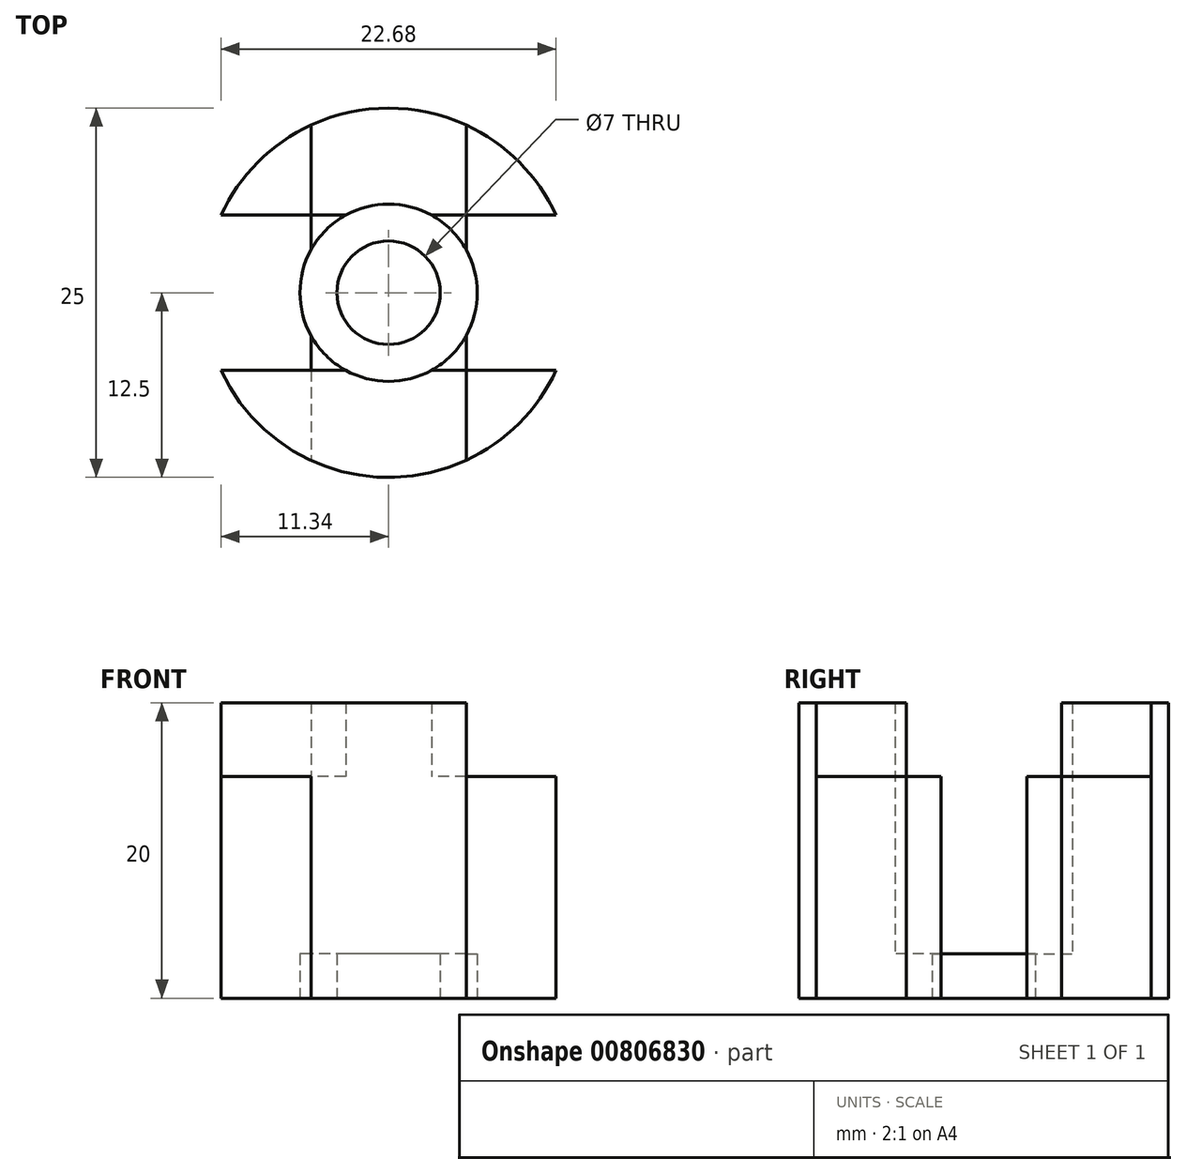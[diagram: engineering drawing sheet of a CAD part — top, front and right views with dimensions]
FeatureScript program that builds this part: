
annotation { "Feature Type Name" : "Feature", "Feature Type Description" : "" }
export const myFeature = defineFeature(function(context is Context, id is Id, definition is map)
    precondition{}
    {
        {
            var Q0;
            Q0=qCreatedBy(makeId("Top.planeOp"),FACE);
            var sketch = newSketch(context, id + "F0", { "sketchPlane" : qUnion([Q0])});
            skCircle(sketch, "E0", {"center": v(0, 0) * mm, "radius": 12.5 * mm});
            skCircle(sketch, "E1", {"center": v(0, 0) * mm, "radius": 6 * mm});
            skLineSegment(sketch, "E2.bottom", {"start": v(5.25, 21.3) * mm, "end": v(-5.25, 21.3) * mm});
            skLineSegment(sketch, "E2.top", {"start": v(5.25, -21.3) * mm, "end": v(-5.25, -21.3) * mm});
            skLineSegment(sketch, "E2.left", {"start": v(5.25, 21.3) * mm, "end": v(5.25, -21.3) * mm});
            skLineSegment(sketch, "E2.right", {"start": v(-5.25, 21.3) * mm, "end": v(-5.25, -21.3) * mm});
            skLineSegment(sketch, "E3.bottom", {"start": v(25.07, 5.25) * mm, "end": v(-25.07, 5.25) * mm});
            skLineSegment(sketch, "E3.top", {"start": v(25.07, -5.25) * mm, "end": v(-25.07, -5.25) * mm});
            skLineSegment(sketch, "E3.left", {"start": v(25.07, 5.25) * mm, "end": v(25.07, -5.25) * mm});
            skLineSegment(sketch, "E3.right", {"start": v(-25.07, 5.25) * mm, "end": v(-25.07, -5.25) * mm});
            skCircle(sketch, "E4", {"center": v(0, 0) * mm, "radius": 3.5 * mm});
            skSolve(sketch);
        }
        {
            var Q0;
            Q0=makeQuery(id+"F0.imprint","IMPRINT",FACE,{"disambiguationData":[TD([[makeQuery(id+"F0.imprint","IMPRINT",EDGE,{"derivedFrom":sQuery(id+"F0.wireOp",EDGE,"E0")}),1.0]])]});
            var Q1;
            {var subQ0=sQuery(id+"F0.wireOp",EDGE,"E3.bottom");var subQ1=sQuery(id+"F0.wireOp",EDGE,"E0");var subQ2=makeQuery(id+"F0.imprint","INTERSECT",VERTEX,{"disambiguationData":[OD(1.0)],"derivedFrom":[subQ1,subQ0]});Q1=makeQuery(id+"F0.imprint","IMPRINT",FACE,{"disambiguationData":[TD([[makeQuery(id+"F0.imprint","IMPRINT",EDGE,{"disambiguationData":[TD([[subQ2,-1.0]])],"derivedFrom":subQ1}),1.0]])]});}
            var Q2;
            {var subQ0=sQuery(id+"F0.wireOp",EDGE,"E2.right");var subQ1=sQuery(id+"F0.wireOp",EDGE,"E0");var subQ2=makeQuery(id+"F0.imprint","INTERSECT",VERTEX,{"disambiguationData":[OD(1.0)],"derivedFrom":[subQ1,subQ0]});Q2=makeQuery(id+"F0.imprint","IMPRINT",FACE,{"disambiguationData":[TD([[makeQuery(id+"F0.imprint","IMPRINT",EDGE,{"disambiguationData":[TD([[subQ2,-1.0]])],"derivedFrom":subQ1}),1.0]])]});}
            var Q3;
            {var subQ0=sQuery(id+"F0.wireOp",EDGE,"E3.bottom");var subQ1=sQuery(id+"F0.wireOp",EDGE,"E0");var subQ2=makeQuery(id+"F0.imprint","INTERSECT",VERTEX,{"disambiguationData":[OD(0.0)],"derivedFrom":[subQ1,subQ0]});Q3=makeQuery(id+"F0.imprint","IMPRINT",FACE,{"disambiguationData":[TD([[makeQuery(id+"F0.imprint","IMPRINT",EDGE,{"disambiguationData":[TD([[subQ2,1.0]])],"derivedFrom":subQ1}),1.0]])]});}
            var Q4;
            {var subQ0=sQuery(id+"F0.wireOp",EDGE,"E2.left");var subQ1=sQuery(id+"F0.wireOp",EDGE,"E0");var subQ2=makeQuery(id+"F0.imprint","INTERSECT",VERTEX,{"disambiguationData":[OD(0.0)],"derivedFrom":[subQ1,subQ0]});Q4=makeQuery(id+"F0.imprint","IMPRINT",FACE,{"disambiguationData":[TD([[makeQuery(id+"F0.imprint","IMPRINT",EDGE,{"disambiguationData":[TD([[subQ2,-1.0]])],"derivedFrom":subQ1}),1.0]])]});}
            var Q5;
            Q5=makeQuery(id+"F0.imprint","IMPRINT",FACE,{"disambiguationData":[TD([[makeQuery(id+"F0.imprint","IMPRINT",EDGE,{"derivedFrom":sQuery(id+"F0.wireOp",EDGE,"E1")}),-1.0]])]});
            extrude(context, id + "F1", {"entities" : qUnion([Q0, Q1, Q2, Q3, Q4, Q5]), "depth" : 15 * mm, "offsetDistance" : 25 * mm});
        }
        {
            var Q0;
            {var subQ0=sQuery(id+"F0.wireOp",EDGE,"E2.right");var subQ1=sQuery(id+"F0.wireOp",EDGE,"E0");var subQ2=makeQuery(id+"F0.imprint","INTERSECT",VERTEX,{"disambiguationData":[OD(0.0)],"derivedFrom":[subQ1,subQ0]});Q0=makeQuery(id+"F0.imprint","IMPRINT",FACE,{"disambiguationData":[TD([[makeQuery(id+"F0.imprint","IMPRINT",EDGE,{"disambiguationData":[TD([[subQ2,-1.0]])],"derivedFrom":subQ1}),1.0]])]});}
            var Q1;
            {var subQ0=sQuery(id+"F0.wireOp",EDGE,"E3.top");var subQ1=sQuery(id+"F0.wireOp",EDGE,"E0");var subQ2=makeQuery(id+"F0.imprint","INTERSECT",VERTEX,{"disambiguationData":[OD(0.0)],"derivedFrom":[subQ1,subQ0]});Q1=makeQuery(id+"F0.imprint","IMPRINT",FACE,{"disambiguationData":[TD([[makeQuery(id+"F0.imprint","IMPRINT",EDGE,{"disambiguationData":[TD([[subQ2,-1.0]])],"derivedFrom":subQ1}),1.0]])]});}
            var Q2;
            {var subQ0=sQuery(id+"F0.wireOp",EDGE,"E2.left");var subQ1=sQuery(id+"F0.wireOp",EDGE,"E0");var subQ2=makeQuery(id+"F0.imprint","INTERSECT",VERTEX,{"disambiguationData":[OD(1.0)],"derivedFrom":[subQ1,subQ0]});Q2=makeQuery(id+"F0.imprint","IMPRINT",FACE,{"disambiguationData":[TD([[makeQuery(id+"F0.imprint","IMPRINT",EDGE,{"disambiguationData":[TD([[subQ2,-1.0]])],"derivedFrom":subQ1}),1.0]])]});}
            var Q3;
            {var subQ0=sQuery(id+"F0.wireOp",EDGE,"E2.left");var subQ1=sQuery(id+"F0.wireOp",EDGE,"E0");var subQ2=makeQuery(id+"F0.imprint","INTERSECT",VERTEX,{"disambiguationData":[OD(0.0)],"derivedFrom":[subQ1,subQ0]});Q3=makeQuery(id+"F0.imprint","IMPRINT",FACE,{"disambiguationData":[TD([[makeQuery(id+"F0.imprint","IMPRINT",EDGE,{"disambiguationData":[TD([[subQ2,1.0]])],"derivedFrom":subQ1}),1.0]])]});}
            extrude(context, id + "F2", {"entities" : qUnion([Q0, Q1, Q2, Q3]), "depth" : 20 * mm, "offsetDistance" : 25 * mm});
        }
        {
            var Q0;
            Q0=makeQuery(id+"F0.imprint","IMPRINT",FACE,{"disambiguationData":[TD([[makeQuery(id+"F0.imprint","IMPRINT",EDGE,{"derivedFrom":sQuery(id+"F0.wireOp",EDGE,"E4")}),-1.0]])]});
            var Q1;
            {var subQ0=sQuery(id+"F0.wireOp",EDGE,"E3.bottom");var subQ1=sQuery(id+"F0.wireOp",EDGE,"E1");var subQ2=makeQuery(id+"F0.imprint","INTERSECT",VERTEX,{"disambiguationData":[OD(0.0)],"derivedFrom":[subQ1,subQ0]});Q1=makeQuery(id+"F0.imprint","IMPRINT",FACE,{"disambiguationData":[TD([[makeQuery(id+"F0.imprint","IMPRINT",EDGE,{"disambiguationData":[TD([[subQ2,-1.0]])],"derivedFrom":subQ1}),1.0]])]});}
            var Q2;
            {var subQ0=sQuery(id+"F0.wireOp",EDGE,"E2.right");var subQ1=sQuery(id+"F0.wireOp",EDGE,"E1");var subQ2=makeQuery(id+"F0.imprint","INTERSECT",VERTEX,{"disambiguationData":[OD(0.0)],"derivedFrom":[subQ1,subQ0]});Q2=makeQuery(id+"F0.imprint","IMPRINT",FACE,{"disambiguationData":[TD([[makeQuery(id+"F0.imprint","IMPRINT",EDGE,{"disambiguationData":[TD([[subQ2,-1.0]])],"derivedFrom":subQ1}),1.0]])]});}
            var Q3;
            {var subQ0=sQuery(id+"F0.wireOp",EDGE,"E3.top");var subQ1=sQuery(id+"F0.wireOp",EDGE,"E1");var subQ2=makeQuery(id+"F0.imprint","INTERSECT",VERTEX,{"disambiguationData":[OD(0.0)],"derivedFrom":[subQ1,subQ0]});Q3=makeQuery(id+"F0.imprint","IMPRINT",FACE,{"disambiguationData":[TD([[makeQuery(id+"F0.imprint","IMPRINT",EDGE,{"disambiguationData":[TD([[subQ2,-1.0]])],"derivedFrom":subQ1}),1.0]])]});}
            var Q4;
            {var subQ0=sQuery(id+"F0.wireOp",EDGE,"E2.left");var subQ1=sQuery(id+"F0.wireOp",EDGE,"E1");var subQ2=makeQuery(id+"F0.imprint","INTERSECT",VERTEX,{"disambiguationData":[OD(0.0)],"derivedFrom":[subQ1,subQ0]});Q4=makeQuery(id+"F0.imprint","IMPRINT",FACE,{"disambiguationData":[TD([[makeQuery(id+"F0.imprint","IMPRINT",EDGE,{"disambiguationData":[TD([[subQ2,1.0]])],"derivedFrom":subQ1}),1.0]])]});}
            extrude(context, id + "F3", {"entities" : qUnion([Q0, Q1, Q2, Q3, Q4]), "operationType" : NewBodyOperationType.ADD, "depth" : 3 * mm, "offsetDistance" : 25 * mm});
        }
    });
